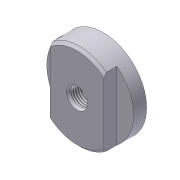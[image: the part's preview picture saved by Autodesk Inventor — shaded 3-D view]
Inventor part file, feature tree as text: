
AUTODESK INVENTOR PART (.ipt)
format: ipt  version: 2013 (Build 170138000, 138)  size: 108,544 bytes
history: native  units: in
note: dims shown in document units (in); Inventor stores cm internally (conversion verified against a paired STEP export)
features: extrude x2, sketch x2, hole x1, chamfer x1
ambient origin geometry x8: Origin, YZ Plane, XZ Plane, XY Plane, X Axis, Y Axis, Z Axis, Center Point
bodies: Solid1 (feature_tree)
feature tree (6):
  extrude  "Extrusion1"  Depth=0.312in TaperAngle=0.0deg
  extrude  "Extrusion2"  Depth=0.312in TaperAngle=0.0deg
  hole  "Hole1"  [1 undecoded]
  chamfer  "Chamfer1"  Distance=0.0625in Angle=45.0deg
  sketch  "Sketch1"  dims[d0=2.062in d1=0.312in d2=0.0in]
  sketch  "Sketch2"  dims[d5=1.272in d6=0.312in d7=0.0in d8=1.0in d9=1.0in d10=0.422in d11=0.395in d12=0.0246in d13=0.423in d14=0.5in d15=0.25in d16=45.0deg d17=0.75in d18=0.8108in d19=0.0625in d20=0.125in d21=45.0deg]
note: 1 required parameter value undecoded (feature->parameter linkage not recoverable at this tier; creation-order binding heuristic only, values carry confidence <= 0.55)
